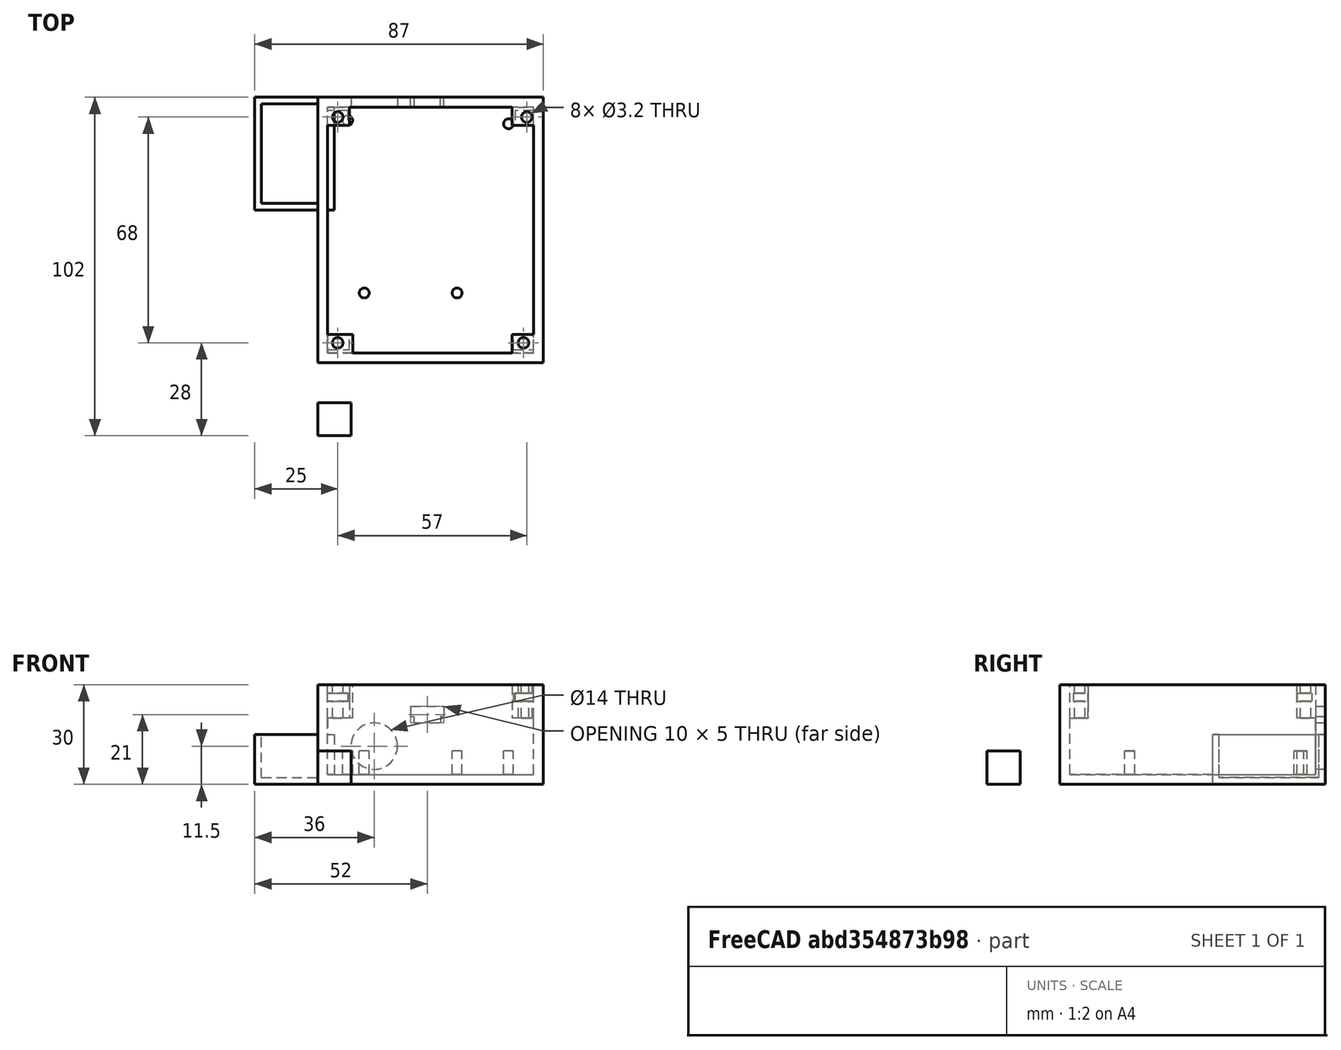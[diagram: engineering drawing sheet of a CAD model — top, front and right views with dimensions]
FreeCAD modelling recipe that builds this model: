
FCSTD DOCUMENT  (FreeCAD 0.19R24276 (Git))
Label: cajaJoystick
License: All rights reserved
LicenseURL: http://en.wikipedia.org/wiki/All_rights_reserved
objects: Part::Box×18, Part::Cut×10, Part::Cylinder×9, Part::MultiFuse×6, Mesh::Feature×3
note: 43 computed .brp shape members not serialized (recipe doc carries the construction recipe); baked Part::Feature solids carry a one-line shape summary decoded from their .brp

FEATURE [Part::Cylinder] Cylinder  label="Cilindro"
  Angle = 360
  AttacherType = Attacher::AttachEngine3D
  Height = 10
  Placement = pos=(14,43,0) rot=(0,0,1;0rad)
  Radius = 1.5
FEATURE [Part::Cylinder] Cylinder001  label="Cilindro001"
  Angle = 360
  AttacherType = Attacher::AttachEngine3D
  Height = 10
  Placement = pos=(42,43,0) rot=(0,0,1;0rad)
  Radius = 1.5
FEATURE [Part::Cylinder] Cylinder002  label="Cilindro002"
  Angle = 360
  AttacherType = Attacher::AttachEngine3D
  Height = 10
  Placement = pos=(57.5,94,0) rot=(0,0,1;0rad)
  Radius = 1.5
FEATURE [Part::Cylinder] Cylinder003  label="Cilindro003"
  Angle = 360
  AttacherType = Attacher::AttachEngine3D
  Height = 10
  Placement = pos=(9,95,0) rot=(0,0,1;0rad)
  Radius = 1.5
FEATURE [Mesh::Feature] nano_expansion_shield_1_  label="nano_expansion_shield(1)"
  Placement = pos=(6,97,5) rot=(0,0,1;-1.5708rad)
FEATURE [Mesh::Feature] Arduino_NANO
  Placement = pos=(33,76,18) rot=(0,0,1;3.14159rad)
FEATURE [Part::Box] Box  label="Cube"
  AttacherType = Attacher::AttachEngine3D
  Height = 3
  Length = 65
  Placement = pos=(0,22,0) rot=(0,0,1;0rad)
  Width = 78
FEATURE [Part::MultiFuse] Fusion
  Shapes = -> [Cylinder,Cylinder001,Cylinder002,Cylinder003,Box]
FEATURE [Part::Box] Box001  label="Cube001"
  AttacherType = Attacher::AttachEngine3D
  Height = 30
  Length = 65
  Placement = pos=(0,22,0) rot=(0,0,1;0rad)
  Width = 3
FEATURE [Part::Box] Box002  label="Cube002"
  AttacherType = Attacher::AttachEngine3D
  Height = 30
  Length = 65
  Placement = pos=(0,99,0) rot=(0,0,1;0rad)
  Width = 3
FEATURE [Part::Box] Box003  label="Cube003"
  AttacherType = Attacher::AttachEngine3D
  Height = 30
  Length = 3
  Placement = pos=(0,22,0) rot=(0,0,1;0rad)
  Width = 80
FEATURE [Part::Box] Box004  label="Cube004"
  AttacherType = Attacher::AttachEngine3D
  Height = 30
  Length = 3
  Placement = pos=(65,22,0) rot=(0,0,1;0rad)
  Width = 80
FEATURE [Part::Box] Box008  label="Cubo008"
  AttacherType = Attacher::AttachEngine3D
  Height = 3
  Length = 10
  Placement = pos=(28,96,20) rot=(0,0,1;0rad)
  Width = 10
FEATURE [Part::Cylinder] Cylinder008  label="Cilindro008"
  Angle = 360
  AttacherType = Attacher::AttachEngine3D
  Height = 10
  Placement = pos=(17,106,12) rot=(1,0,0;1.5708rad)
  Radius = 7
FEATURE [Part::Box] Box007  label="Cubo007"
  AttacherType = Attacher::AttachEngine3D
  Height = 3
  Length = 8
  Placement = pos=(29,96,18) rot=(0,0,1;0rad)
  Width = 10
FEATURE [Part::MultiFuse] Fusion001006
  Placement = pos=(0,0,1) rot=(0,0,1;0rad)
  Shapes = -> [Box007,Box008]
FEATURE [Part::MultiFuse] Fusion001005
  Placement = pos=(0,1,-0.5) rot=(0,0,1;0rad)
  Shapes = -> [Cylinder008,Fusion001006]
FEATURE [Part::Cut] Cut
  Base = -> Box002
  Tool = -> Fusion001005
FEATURE [Part::MultiFuse] Fusion001007  label="caja"
  Shapes = -> [Cut,Box004,Box003,Box001,Fusion]
FEATURE [Part::Box] Box009  label="Cube005"
  AttacherType = Attacher::AttachEngine3D
  Height = 10
  Length = 8
  Placement = pos=(2.5,25.5,15) rot=(0,0,1;0rad)
  Width = 6
FEATURE [Part::Box] Box010  label="Cube006"
  AttacherType = Attacher::AttachEngine3D
  Height = 2.5
  Length = 6.5
  Placement = pos=(3,27,20) rot=(0,0,1;0rad)
  Width = 5
FEATURE [Part::Cut] Cut001
  Base = -> Box009
  Tool = -> Box010
FEATURE [Part::Cylinder] Cylinder009  label="Cylinder"
  Angle = 360
  AttacherType = Attacher::AttachEngine3D
  Height = 30
  Placement = pos=(6,29,0) rot=(0,0,1;0rad)
  Radius = 1.6
FEATURE [Part::Cut] Cut002
  Base = -> Cut001
  Placement = pos=(0,-1,5) rot=(0,0,1;0rad)
  Tool = -> Cylinder009
FEATURE [Part::Box] Box011  label="Cube007"
  AttacherType = Attacher::AttachEngine3D
  Height = 10
  Length = 8
  Placement = pos=(2.5,25.5,15) rot=(0,0,1;0rad)
  Width = 6
FEATURE [Part::Box] Box012  label="Cube008"
  AttacherType = Attacher::AttachEngine3D
  Height = 2.5
  Length = 6.5
  Placement = pos=(3,27,20) rot=(0,0,1;0rad)
  Width = 5
FEATURE [Part::Cylinder] Cylinder010
  Angle = 360
  AttacherType = Attacher::AttachEngine3D
  Height = 30
  Placement = pos=(6,29,0) rot=(0,0,1;0rad)
  Radius = 1.6
FEATURE [Part::Cut] Cut004
  Base = -> Box011
  Tool = -> Box012
FEATURE [Part::Cut] Cut003
  Base = -> Cut004
  Placement = pos=(56,-1,5) rot=(0,0,1;0rad)
  Tool = -> Cylinder010
FEATURE [Part::Box] Box013  label="Cube009"
  AttacherType = Attacher::AttachEngine3D
  Height = 2.5
  Length = 6.5
  Placement = pos=(3,27,20) rot=(0,0,1;0rad)
  Width = 5
FEATURE [Part::Cylinder] Cylinder011
  Angle = 360
  AttacherType = Attacher::AttachEngine3D
  Height = 30
  Placement = pos=(6,29,0) rot=(0,0,1;0rad)
  Radius = 1.6
FEATURE [Part::Box] Box014  label="Cube010"
  AttacherType = Attacher::AttachEngine3D
  Height = 10
  Length = 8
  Placement = pos=(2.5,25.5,15) rot=(0,0,1;0rad)
  Width = 6
FEATURE [Part::Cut] Cut005
  Base = -> Box014
  Tool = -> Box013
FEATURE [Part::Cut] Cut006
  Base = -> Cut005
  Placement = pos=(69,125,5) rot=(0,0,1;3.14159rad)
  Tool = -> Cylinder011
FEATURE [Part::Box] Box015  label="Cube011"
  AttacherType = Attacher::AttachEngine3D
  Height = 2.5
  Length = 6.5
  Placement = pos=(3,27,20) rot=(0,0,1;0rad)
  Width = 5
FEATURE [Part::Box] Box016  label="Cube012"
  AttacherType = Attacher::AttachEngine3D
  Height = 10
  Length = 8
  Placement = pos=(2.5,25.5,15) rot=(0,0,1;0rad)
  Width = 6
FEATURE [Part::Cut] Cut008
  Base = -> Box016
  Tool = -> Box015
FEATURE [Part::Cylinder] Cylinder012
  Angle = 360
  AttacherType = Attacher::AttachEngine3D
  Height = 30
  Placement = pos=(6,29,0) rot=(0,0,1;0rad)
  Radius = 1.6
FEATURE [Part::Cut] Cut007
  Base = -> Cut008
  Placement = pos=(12,125,5) rot=(0,0,1;3.14159rad)
  Tool = -> Cylinder012
FEATURE [Part::MultiFuse] Fusion001008
  Shapes = -> [Cut007,Cut006,Cut003,Cut002,Fusion001007]
FEATURE [Part::Box] Box017  label="Cube013"
  AttacherType = Attacher::AttachEngine3D
  Height = 10
  Length = 10
  Width = 10
FEATURE [Part::Box] Box018  label="Cube014"
  AttacherType = Attacher::AttachEngine3D
  Height = 15
  Length = 24
  Placement = pos=(-19,68,0) rot=(0,0,1;0rad)
  Width = 34
FEATURE [Part::Box] Box019  label="Cube015"
  AttacherType = Attacher::AttachEngine3D
  Height = 15
  Length = 20
  Placement = pos=(-17,70,2) rot=(0,0,1;0rad)
  Width = 30
FEATURE [Part::Cut] Cut009
  Base = -> Box018
  Tool = -> Box019
FEATURE [Part::MultiFuse] Fusion001009
  Shapes = -> [Fusion001008,Cut009]
FEATURE [Mesh::Feature] Mesh  label="Fusion001009 (Meshed)"
